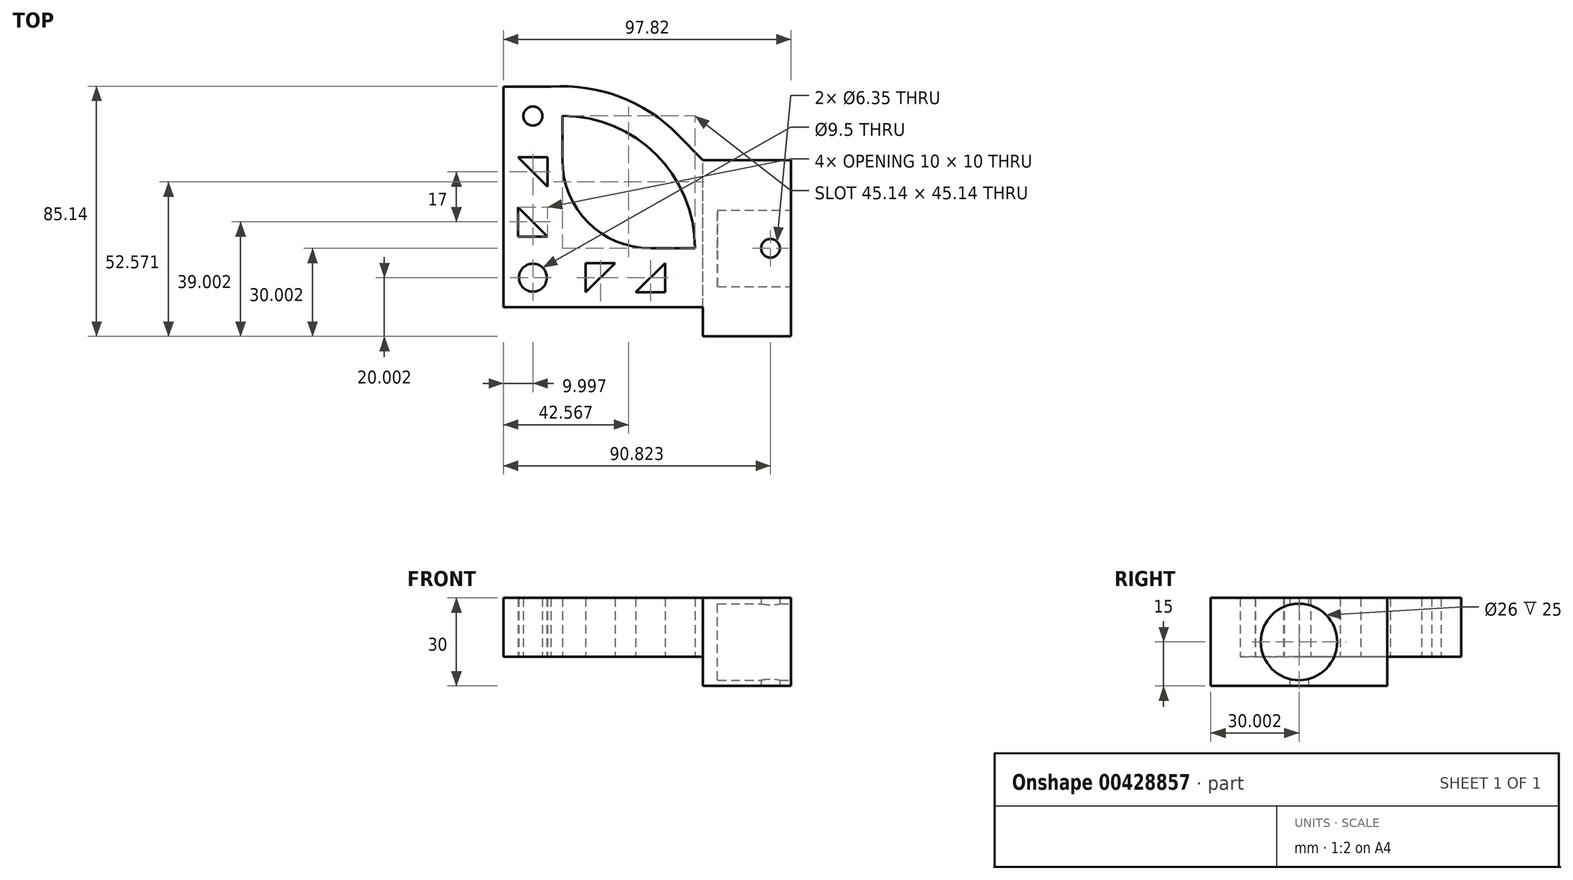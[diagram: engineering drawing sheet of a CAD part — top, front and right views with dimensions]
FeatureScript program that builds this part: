
annotation { "Feature Type Name" : "Feature", "Feature Type Description" : "" }
export const myFeature = defineFeature(function(context is Context, id is Id, definition is map)
    precondition{}
    {
        {
            var Q0;
            Q0=qCreatedBy(makeId("Top.planeOp"),FACE);
            var sketch = newSketch(context, id + "F0", { "sketchPlane" : qUnion([Q0])});
            skLineSegment(sketch, "E0.bottom", {"start": v(-28.36, 53.91) * mm, "end": v(-8.36, 53.91) * mm});
            skLineSegment(sketch, "E0.top", {"start": v(-28.36, -21.09) * mm, "end": v(-8.36, -21.09) * mm});
            skLineSegment(sketch, "E0.left", {"start": v(-28.36, 53.91) * mm, "end": v(-28.36, -21.09) * mm});
            skLineSegment(sketch, "E0.right", {"start": v(-8.36, 53.91) * mm, "end": v(-8.36, 28.91) * mm});
            skLineSegment(sketch, "E1.left", {"start": v(-8.36, -1.09) * mm, "end": v(-8.36, -21.09) * mm});
            skCircle(sketch, "E2", {"center": v(-18.36, -11.09) * mm, "radius": 4.75 * mm});
            skCircle(sketch, "E3", {"center": v(-18.36, 43.91) * mm, "radius": 3.25 * mm});
            skLineSegment(sketch, "E4", {"start": v(16.64, -16.09) * mm, "end": v(26.64, -6.09) * mm});
            skLineSegment(sketch, "E5", {"start": v(26.64, -6.09) * mm, "end": v(26.64, -16.09) * mm});
            skLineSegment(sketch, "E6", {"start": v(26.64, -16.09) * mm, "end": v(16.64, -16.09) * mm});
            skLineSegment(sketch, "E7", {"start": v(9.64, -6.09) * mm, "end": v(-0.36, -16.09) * mm});
            skLineSegment(sketch, "E8", {"start": v(-0.36, -16.09) * mm, "end": v(-0.36, -6.09) * mm});
            skLineSegment(sketch, "E9", {"start": v(-0.36, -6.09) * mm, "end": v(9.64, -6.09) * mm});
            skLineSegment(sketch, "E10", {"start": v(-13.36, 19.91) * mm, "end": v(-23.36, 29.91) * mm});
            skLineSegment(sketch, "E11", {"start": v(-23.36, 29.91) * mm, "end": v(-13.36, 29.91) * mm});
            skLineSegment(sketch, "E12", {"start": v(-13.36, 29.91) * mm, "end": v(-13.36, 19.91) * mm});
            skLineSegment(sketch, "E13", {"start": v(-23.36, 12.91) * mm, "end": v(-13.36, 2.91) * mm});
            skLineSegment(sketch, "E14", {"start": v(-13.36, 2.91) * mm, "end": v(-23.36, 2.91) * mm});
            skLineSegment(sketch, "E15", {"start": v(-23.36, 2.91) * mm, "end": v(-23.36, 12.91) * mm});
            skArc(sketch, "E16.filletArc", {"start": v(-8.36, 28.91) * mm, "mid": v(0.42, 7.7) * mm, "end": v(21.64, -1.09) * mm});
            skLineSegment(sketch, "E17.bottom", {"start": v(39.46, -31.09) * mm, "end": v(69.46, -31.09) * mm});
            skLineSegment(sketch, "E17.top", {"start": v(39.46, 28.91) * mm, "end": v(69.46, 28.91) * mm});
            skLineSegment(sketch, "E17.right", {"start": v(69.46, -31.09) * mm, "end": v(69.46, 28.91) * mm});
            skLineSegment(sketch, "E18", {"start": v(-8.36, -21.09) * mm, "end": v(39.46, -21.09) * mm});
            skLineSegment(sketch, "E19", {"start": v(39.46, -1.09) * mm, "end": v(21.64, -1.09) * mm});
            skCircle(sketch, "E20", {"center": v(-8.36, -1.09) * mm, "radius": 55.14 * mm});
            skCircle(sketch, "E21", {"center": v(-8.36, -1.09) * mm, "radius": 45.14 * mm});
            skLineSegment(sketch, "E22", {"start": v(39.46, 28.91) * mm, "end": v(30.97, 37.56) * mm});
            skLineSegment(sketch, "E23", {"start": v(39.46, -1.09) * mm, "end": v(39.46, 28.91) * mm});
            skLineSegment(sketch, "E24", {"start": v(39.46, -21.09) * mm, "end": v(39.46, -31.09) * mm});
            skCircle(sketch, "E25", {"center": v(62.46, -1.09) * mm, "radius": 3.18 * mm});
            skLineSegment(sketch, "E26", {"start": v(39.46, -1.09) * mm, "end": v(39.46, -21.09) * mm});
            skSolve(sketch);
        }
        {
            var Q0;
            {var subQ5=sQuery(id+"F0.wireOp",EDGE,"E17.bottom");Q0=makeQuery(id+"F0.imprint","IMPRINT",FACE,{"disambiguationData":[TD([[makeQuery(id+"F0.imprint","IMPRINT",EDGE,{"derivedFrom":subQ5}),1.0]])]});}
            var Q1;
            {var subQ5=sQuery(id+"F0.wireOp",EDGE,"E26");Q1=makeQuery(id+"F0.imprint","IMPRINT",FACE,{"disambiguationData":[TD([[makeQuery(id+"F0.imprint","IMPRINT",EDGE,{"derivedFrom":subQ5}),1.0]])]});}
            var Q2;
            {var subQ1=sQuery(id+"F0.wireOp",EDGE,"E0.top");Q2=makeQuery(id+"F0.imprint","IMPRINT",FACE,{"disambiguationData":[TD([[makeQuery(id+"F0.imprint","IMPRINT",EDGE,{"derivedFrom":subQ1}),1.0]])]});}
            var Q3;
            {var subQ0=sQuery(id+"F0.wireOp",EDGE,"E26");Q3=makeQuery(id+"F0.imprint","IMPRINT",FACE,{"disambiguationData":[TD([[makeQuery(id+"F0.imprint","IMPRINT",EDGE,{"derivedFrom":subQ0}),-1.0]])]});}
            var Q4;
            {var subQ8=sQuery(id+"F0.wireOp",EDGE,"E0.right");var subQ9=sQuery(id+"F0.wireOp",EDGE,"E0.bottom");var subQ10=makeQuery(id+"F0.imprint","INTERSECT",VERTEX,{"derivedFrom":[subQ9,subQ8]});Q4=makeQuery(id+"F0.imprint","IMPRINT",FACE,{"disambiguationData":[TD([[makeQuery(id+"F0.imprint","IMPRINT",EDGE,{"disambiguationData":[TD([[subQ10,1.0]])],"derivedFrom":subQ9}),1.0]])]});}
            var Q5;
            {var subQ8=sQuery(id+"F0.wireOp",EDGE,"E0.right");var subQ10=sQuery(id+"F0.wireOp",EDGE,"E0.bottom");var subQ11=makeQuery(id+"F0.imprint","INTERSECT",VERTEX,{"derivedFrom":[subQ10,subQ8]});Q5=makeQuery(id+"F0.imprint","IMPRINT",FACE,{"disambiguationData":[TD([[makeQuery(id+"F0.imprint","IMPRINT",EDGE,{"disambiguationData":[TD([[subQ11,1.0]])],"derivedFrom":subQ10}),-1.0]])]});}
            var Q6;
            {var subQ0=sQuery(id+"F0.wireOp",EDGE,"E0.left");var subQ1=sQuery(id+"F0.wireOp",EDGE,"E0.bottom");var subQ2=makeQuery(id+"F0.imprint","INTERSECT",VERTEX,{"derivedFrom":[subQ1,subQ0]});Q6=makeQuery(id+"F0.imprint","IMPRINT",FACE,{"disambiguationData":[TD([[makeQuery(id+"F0.imprint","IMPRINT",EDGE,{"disambiguationData":[TD([[subQ2,-1.0]])],"derivedFrom":subQ1}),-1.0]])]});}
            var Q7;
            {var subQ0=sQuery(id+"F0.wireOp",EDGE,"E22");Q7=makeQuery(id+"F0.imprint","IMPRINT",FACE,{"disambiguationData":[TD([[makeQuery(id+"F0.imprint","IMPRINT",EDGE,{"derivedFrom":subQ0}),1.0]])]});}
            extrude(context, id + "F1", {"entities" : qUnion([Q0, Q1, Q2, Q3, Q4, Q5, Q6, Q7]), "depth" : 20 * mm});
        }
        {
            var Q0;
            {var subQ5=sQuery(id+"F0.wireOp",EDGE,"E17.bottom");Q0=makeQuery(id+"F0.imprint","IMPRINT",FACE,{"disambiguationData":[TD([[makeQuery(id+"F0.imprint","IMPRINT",EDGE,{"derivedFrom":subQ5}),1.0]])]});}
            var Q1;
            {var subQ5=sQuery(id+"F0.wireOp",EDGE,"E26");Q1=makeQuery(id+"F0.imprint","IMPRINT",FACE,{"disambiguationData":[TD([[makeQuery(id+"F0.imprint","IMPRINT",EDGE,{"derivedFrom":subQ5}),1.0]])]});}
            extrude(context, id + "F2", {"entities" : qUnion([Q0, Q1]), "operationType" : NewBodyOperationType.ADD, "oppositeDirection" : true, "depth" : 10 * mm});
        }
        {
            var Q0;
            {var subQ0=sQuery(id+"F0.wireOp",EDGE,"E17.right");Q0=makeQuery(id+"F2.boolean.opBoolean","MERGE",FACE,{"derivedFrom":[makeQuery(id+"F1.opExtrude","SWEPT_FACE",FACE,{"disambiguationData":[OSD([subQ0])]}),makeQuery(id+"F2.opExtrude","SWEPT_FACE",FACE,{"disambiguationData":[OSD([subQ0])]})]});}
            var sketch = newSketch(context, id + "F3", { "sketchPlane" : qUnion([Q0])});
            skCircle(sketch, "E27", {"center": v(-1.09, 5) * mm, "radius": 13 * mm});
            skSolve(sketch);
        }
        {
            var Q0;
            Q0 = qSketchRegion(id + "F3", true);
            extrude(context, id + "F4", {"entities" : qUnion([Q0]), "operationType" : NewBodyOperationType.REMOVE, "oppositeDirection" : true, "depth" : 25 * mm});
        }
    });
